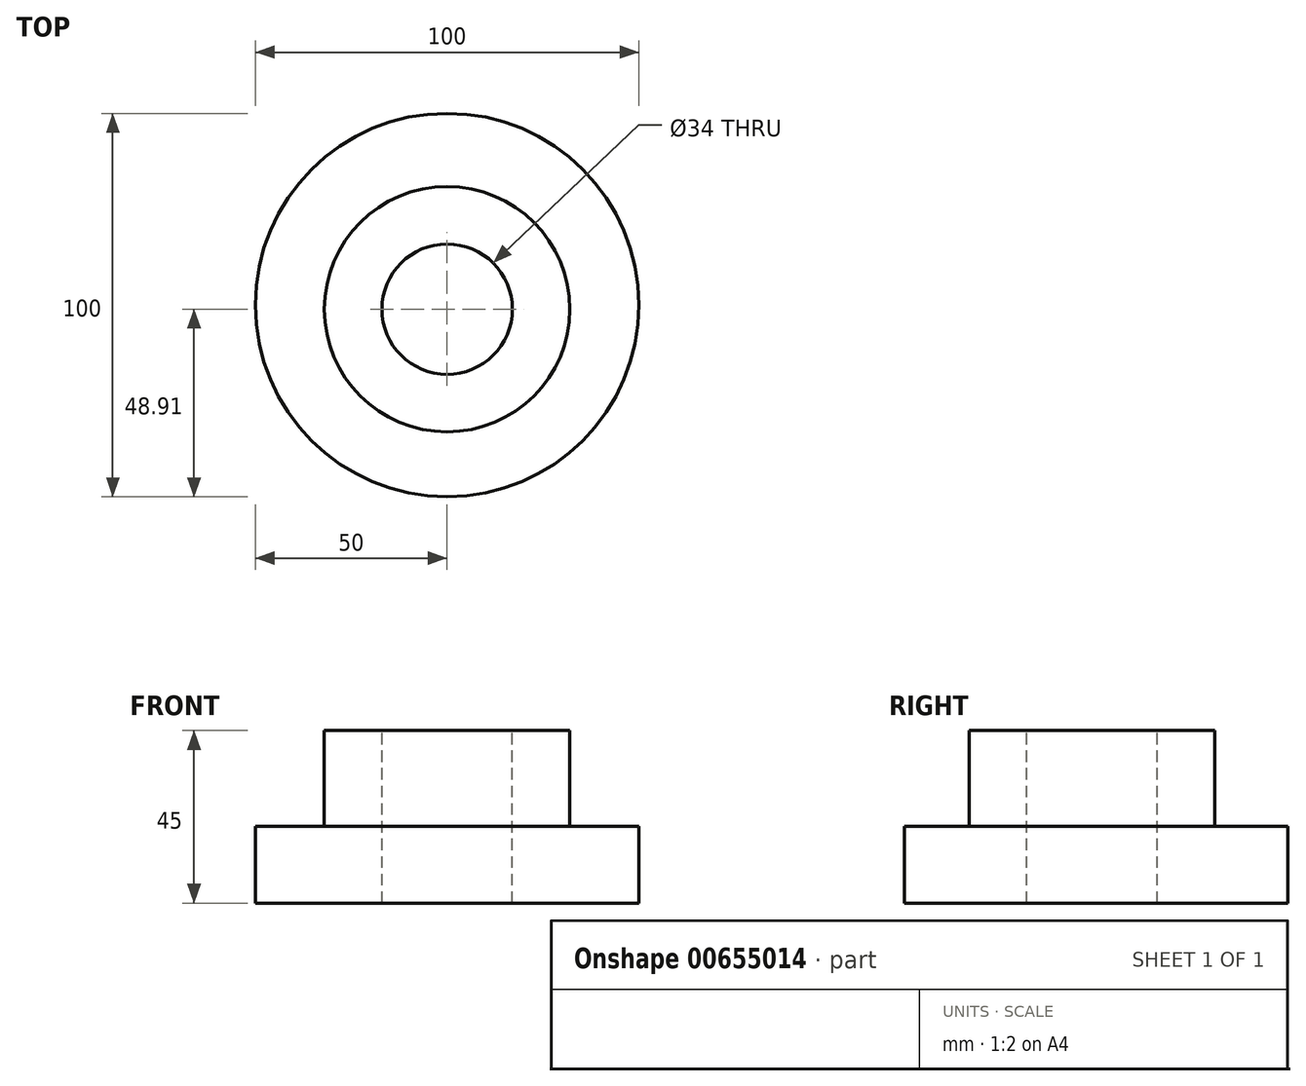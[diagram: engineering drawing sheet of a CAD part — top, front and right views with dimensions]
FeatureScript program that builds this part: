
annotation { "Feature Type Name" : "Feature", "Feature Type Description" : "" }
export const myFeature = defineFeature(function(context is Context, id is Id, definition is map)
    precondition{}
    {
        {
            var Q0;
            Q0=qCreatedBy(makeId("Top.planeOp"),FACE);
            var sketch = newSketch(context, id + "F0", { "sketchPlane" : qUnion([Q0])});
            skCircle(sketch, "E0", {"center": v(0, 1.09) * mm, "radius": 50 * mm});
            skSolve(sketch);
        }
        {
            var Q0;
            Q0=makeQuery(id+"F0.imprint","IMPRINT",FACE,{"disambiguationData":[TD([[makeQuery(id+"F0.imprint","IMPRINT",EDGE,{"derivedFrom":sQuery(id+"F0.wireOp",EDGE,"E0")}),1.0]])]});
            extrude(context, id + "F1", {"entities" : qUnion([Q0]), "depth" : 20 * mm, "offsetDistance" : 25 * mm});
        }
        {
            var Q0;
            Q0=makeQuery(id+"F1.opExtrude","CAP_FACE",FACE,{"disambiguationData":[OSD([sQuery(id+"F0.wireOp",EDGE,"E0")])],"isStart":false});
            var sketch = newSketch(context, id + "F2", { "sketchPlane" : qUnion([Q0])});
            skCircle(sketch, "E1", {"center": v(0, 0) * mm, "radius": 32 * mm});
            skSolve(sketch);
        }
        {
            var Q0;
            Q0=makeQuery(id+"F2.imprint","IMPRINT",FACE,{"disambiguationData":[TD([[makeQuery(id+"F2.imprint","IMPRINT",EDGE,{"derivedFrom":sQuery(id+"F2.wireOp",EDGE,"E1")}),1.0]])]});
            extrude(context, id + "F3", {"entities" : qUnion([Q0]), "operationType" : NewBodyOperationType.ADD, "depth" : 25 * mm, "offsetDistance" : 25 * mm});
        }
        {
            var Q0;
            Q0=makeQuery(id+"F3.opExtrude","CAP_FACE",FACE,{"disambiguationData":[OSD([sQuery(id+"F2.wireOp",EDGE,"E1")])],"isStart":false});
            var sketch = newSketch(context, id + "F4", { "sketchPlane" : qUnion([Q0])});
            skPoint(sketch, "E2", {"position": v(0, 0) * mm});
            skSolve(sketch);
        }
        {
            var Q0;
            Q0=sQuery(id+"F4.wireOp",VERTEX,"E2");
            var Q1;
            Q1=makeQuery(id+"F1.opExtrude","SWEPT_BODY",BODY,{"disambiguationData":[OSD([sQuery(id+"F0.wireOp",EDGE,"E0")])]});
            hole(context, id + "F5", {"style" : HoleStyle.SIMPLE, "endStyle" : HoleEndStyle.THROUGH, "holeDiameter" : 34 * mm, "majorDiameter" : 5 * mm, "isTappedThrough" : true, "tappedDepth" : 12 * mm, "tapClearance" : 3, "locations" : qUnion([Q0]), "scope" : qUnion([Q1])});
        }
    });
